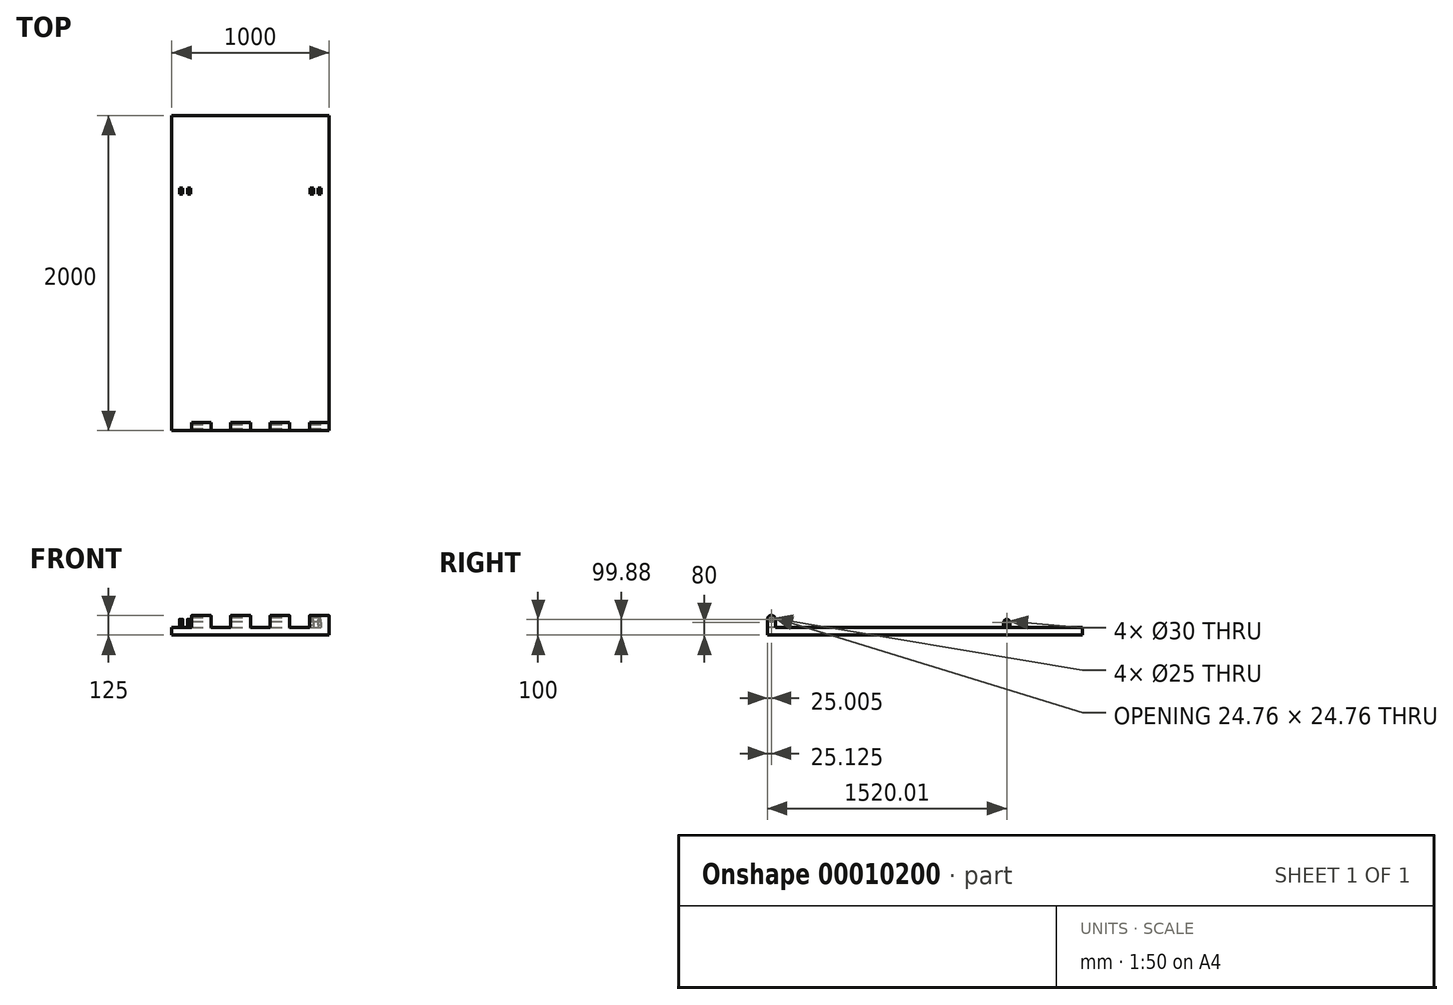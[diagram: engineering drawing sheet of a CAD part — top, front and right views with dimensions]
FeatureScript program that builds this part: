
annotation { "Feature Type Name" : "Feature", "Feature Type Description" : "" }
export const myFeature = defineFeature(function(context is Context, id is Id, definition is map)
    precondition{}
    {
        {
            var Q0;
            Q0=qCreatedBy(makeId("Top.planeOp"),FACE);
            var sketch = newSketch(context, id + "F0", { "sketchPlane" : qUnion([Q0])});
            skLineSegment(sketch, "E0.bottom", {"start": v(-409.07, -956.56) * mm, "end": v(590.93, -956.56) * mm});
            skLineSegment(sketch, "E0.top", {"start": v(-409.07, 1043.44) * mm, "end": v(590.93, 1043.44) * mm});
            skLineSegment(sketch, "E0.left", {"start": v(-409.07, -956.56) * mm, "end": v(-409.07, 1043.44) * mm});
            skLineSegment(sketch, "E0.right", {"start": v(590.93, -956.56) * mm, "end": v(590.93, 1043.44) * mm});
            skSolve(sketch);
        }
        {
            var Q0;
            Q0=qSketchRegion(id+"F0",true);
            extrude(context, id + "F1", {"entities" : qUnion([Q0]), "depth" : 50 * mm});
        }
        {
            var Q0;
            Q0=makeQuery(id+"F1.opExtrude","SWEPT_FACE",FACE,{"disambiguationData":[OSD([sQuery(id+"F0.wireOp",EDGE,"E0.right")])]});
            var sketch = newSketch(context, id + "F2", { "sketchPlane" : qUnion([Q0])});
            skLineSegment(sketch, "E1.bottom", {"start": v(-956.56, 50) * mm, "end": v(-906.56, 50) * mm});
            skLineSegment(sketch, "E1.left", {"start": v(-956.56, 50) * mm, "end": v(-956.56, 100) * mm});
            skLineSegment(sketch, "E1.right", {"start": v(-906.56, 50) * mm, "end": v(-906.56, 100) * mm});
            skArc(sketch, "E2", {"start": v(-906.56, 100) * mm, "mid": v(-931.56, 125) * mm, "end": v(-956.56, 100) * mm});
            skCircle(sketch, "E3", {"center": v(-931.56, 100) * mm, "radius": 12.5 * mm});
            skSolve(sketch);
        }
        {
            var Q0;
            Q0=qSketchRegion(id+"F2",true);
            extrude(context, id + "F3", {"entities" : qUnion([Q0]), "oppositeDirection" : true, "depth" : 1000 * mm});
        }
        {
            var Q0;
            Q0=makeQuery(id+"F1.opExtrude","CAP_FACE",FACE,{"disambiguationData":[OSD([sQuery(id+"F0.wireOp",EDGE,"E0.bottom"),sQuery(id+"F0.wireOp",EDGE,"E0.top"),sQuery(id+"F0.wireOp",EDGE,"E0.left"),sQuery(id+"F0.wireOp",EDGE,"E0.right")])],"isStart":false});
            var sketch = newSketch(context, id + "F4", { "sketchPlane" : qUnion([Q0])});
            skLineSegment(sketch, "E4.bottom", {"start": v(-159.07, -818.58) * mm, "end": v(-34.07, -818.58) * mm});
            skLineSegment(sketch, "E4.top", {"start": v(-159.07, -1033.47) * mm, "end": v(-34.07, -1033.47) * mm});
            skLineSegment(sketch, "E4.left", {"start": v(-159.07, -818.58) * mm, "end": v(-159.07, -1033.47) * mm});
            skLineSegment(sketch, "E4.right", {"start": v(-34.07, -818.58) * mm, "end": v(-34.07, -1033.47) * mm});
            skLineSegment(sketch, "E5.bottom", {"start": v(90.93, -816.35) * mm, "end": v(215.93, -816.35) * mm});
            skLineSegment(sketch, "E5.top", {"start": v(90.93, -1023.71) * mm, "end": v(215.93, -1023.71) * mm});
            skLineSegment(sketch, "E5.left", {"start": v(90.93, -816.35) * mm, "end": v(90.93, -1023.71) * mm});
            skLineSegment(sketch, "E5.right", {"start": v(215.93, -816.35) * mm, "end": v(215.93, -1023.71) * mm});
            skLineSegment(sketch, "E6.bottom", {"start": v(340.93, -840.14) * mm, "end": v(465.93, -840.14) * mm});
            skLineSegment(sketch, "E6.top", {"start": v(340.93, -1023.71) * mm, "end": v(465.93, -1023.71) * mm});
            skLineSegment(sketch, "E6.left", {"start": v(340.93, -840.14) * mm, "end": v(340.93, -1023.71) * mm});
            skLineSegment(sketch, "E6.right", {"start": v(465.93, -840.14) * mm, "end": v(465.93, -1023.71) * mm});
            skLineSegment(sketch, "E7.bottom", {"start": v(-284.07, -802.65) * mm, "end": v(-409.07, -802.65) * mm});
            skLineSegment(sketch, "E7.top", {"start": v(-284.07, -1062.3) * mm, "end": v(-409.07, -1062.3) * mm});
            skLineSegment(sketch, "E7.left", {"start": v(-284.07, -802.65) * mm, "end": v(-284.07, -1062.3) * mm});
            skLineSegment(sketch, "E7.right", {"start": v(-409.07, -802.65) * mm, "end": v(-409.07, -1062.3) * mm});
            skSolve(sketch);
        }
        {
            var Q0;
            Q0=qSketchRegion(id+"F4",true);
            extrude(context, id + "F5", {"entities" : qUnion([Q0]), "operationType" : NewBodyOperationType.REMOVE, "endBound" : BoundingType.THROUGH_ALL, "depth" : 60 * mm});
        }
        {
            var Q0;
            Q0=makeQuery(id+"F1.opExtrude","SWEPT_BODY",BODY,{"disambiguationData":[OSD([sQuery(id+"F0.wireOp",EDGE,"E0.bottom"),sQuery(id+"F0.wireOp",EDGE,"E0.top"),sQuery(id+"F0.wireOp",EDGE,"E0.left"),sQuery(id+"F0.wireOp",EDGE,"E0.right")])]});
            var Q1;
            Q1=makeQuery(id+"F5.boolean.opBoolean","SPLIT",BODY,{"disambiguationData":[OD(0.0)],"derivedFrom":makeQuery(id+"F3.opExtrude","SWEPT_BODY",BODY,{"disambiguationData":[OSD([sQuery(id+"F2.wireOp",EDGE,"E1.bottom"),sQuery(id+"F2.wireOp",EDGE,"E1.left"),sQuery(id+"F2.wireOp",EDGE,"E1.right"),sQuery(id+"F2.wireOp",EDGE,"E2"),sQuery(id+"F2.wireOp",EDGE,"E3")])]})});
            var Q2;
            Q2=makeQuery(id+"F5.boolean.opBoolean","SPLIT",BODY,{"disambiguationData":[OD(1.0)],"derivedFrom":makeQuery(id+"F3.opExtrude","SWEPT_BODY",BODY,{"disambiguationData":[OSD([sQuery(id+"F2.wireOp",EDGE,"E1.bottom"),sQuery(id+"F2.wireOp",EDGE,"E1.left"),sQuery(id+"F2.wireOp",EDGE,"E1.right"),sQuery(id+"F2.wireOp",EDGE,"E2"),sQuery(id+"F2.wireOp",EDGE,"E3")])]})});
            var Q3;
            Q3=makeQuery(id+"F5.boolean.opBoolean","SPLIT",BODY,{"disambiguationData":[OD(2.0)],"derivedFrom":makeQuery(id+"F3.opExtrude","SWEPT_BODY",BODY,{"disambiguationData":[OSD([sQuery(id+"F2.wireOp",EDGE,"E1.bottom"),sQuery(id+"F2.wireOp",EDGE,"E1.left"),sQuery(id+"F2.wireOp",EDGE,"E1.right"),sQuery(id+"F2.wireOp",EDGE,"E2"),sQuery(id+"F2.wireOp",EDGE,"E3")])]})});
            booleanBodies(context, id + "F6", {"operationType" : BooleanOperationType.UNION, "tools" : qUnion([Q0, Q1, Q2, Q3])});
        }
        {
            var Q0;
            Q0=makeQuery(id+"F6.opBoolean","MERGE",FACE,{"derivedFrom":[makeQuery(id+"F1.opExtrude","SWEPT_FACE",FACE,{"disambiguationData":[OSD([sQuery(id+"F0.wireOp",EDGE,"E0.right")])]}),makeQuery(id+"F3.opExtrude","CAP_FACE",FACE,{"disambiguationData":[OSD([sQuery(id+"F2.wireOp",EDGE,"E1.bottom"),sQuery(id+"F2.wireOp",EDGE,"E1.left"),sQuery(id+"F2.wireOp",EDGE,"E1.right"),sQuery(id+"F2.wireOp",EDGE,"E2"),sQuery(id+"F2.wireOp",EDGE,"E3")])],"isStart":true})]});
            var sketch = newSketch(context, id + "F7", { "sketchPlane" : qUnion([Q0])});
            skLineSegment(sketch, "E8.bottom", {"start": v(543.44, 50) * mm, "end": v(583.44, 50) * mm});
            skLineSegment(sketch, "E8.left", {"start": v(543.44, 50) * mm, "end": v(543.44, 80) * mm});
            skLineSegment(sketch, "E8.right", {"start": v(583.44, 50) * mm, "end": v(583.44, 80) * mm});
            skArc(sketch, "E9", {"start": v(583.44, 80) * mm, "mid": v(563.44, 100) * mm, "end": v(543.44, 80) * mm});
            skCircle(sketch, "E10", {"center": v(563.44, 80) * mm, "radius": 15 * mm});
            skSolve(sketch);
        }
        {
            var Q0;
            Q0=qSketchRegion(id+"F7",true);
            extrude(context, id + "F8", {"entities" : qUnion([Q0]), "oppositeDirection" : true, "depth" : 1000 * mm});
        }
        {
            var Q0;
            Q0=makeQuery(id+"F8.opExtrude","SWEPT_FACE",FACE,{"disambiguationData":[OSD([sQuery(id+"F7.wireOp",EDGE,"E8.bottom")])]});
            var sketch = newSketch(context, id + "F9", { "sketchPlane" : qUnion([Q0])});
            skLineSegment(sketch, "E11.bottom", {"start": v(590.93, -583.44) * mm, "end": v(540.93, -583.44) * mm});
            skLineSegment(sketch, "E11.top", {"start": v(590.93, -383.44) * mm, "end": v(540.93, -383.44) * mm});
            skLineSegment(sketch, "E11.left", {"start": v(590.93, -583.44) * mm, "end": v(590.93, -383.44) * mm});
            skLineSegment(sketch, "E11.right", {"start": v(540.93, -583.44) * mm, "end": v(540.93, -383.44) * mm});
            skLineSegment(sketch, "E12.bottom", {"start": v(520.93, -583.44) * mm, "end": v(490.93, -583.44) * mm});
            skLineSegment(sketch, "E12.top", {"start": v(520.93, -383.44) * mm, "end": v(490.93, -383.44) * mm});
            skLineSegment(sketch, "E12.left", {"start": v(520.93, -583.44) * mm, "end": v(520.93, -383.44) * mm});
            skLineSegment(sketch, "E12.right", {"start": v(490.93, -583.44) * mm, "end": v(490.93, -383.44) * mm});
            skLineSegment(sketch, "E13.bottom", {"start": v(470.93, -383.44) * mm, "end": v(-289.07, -383.44) * mm});
            skLineSegment(sketch, "E13.top", {"start": v(470.93, -583.44) * mm, "end": v(-289.07, -583.44) * mm});
            skLineSegment(sketch, "E13.left", {"start": v(470.93, -583.44) * mm, "end": v(470.93, -383.44) * mm});
            skLineSegment(sketch, "E13.right", {"start": v(-289.07, -583.44) * mm, "end": v(-289.07, -383.44) * mm});
            skLineSegment(sketch, "E14.bottom", {"start": v(-359.07, -583.44) * mm, "end": v(-409.07, -583.44) * mm});
            skLineSegment(sketch, "E14.top", {"start": v(-359.07, -383.44) * mm, "end": v(-409.07, -383.44) * mm});
            skLineSegment(sketch, "E14.left", {"start": v(-359.07, -583.44) * mm, "end": v(-359.07, -383.44) * mm});
            skLineSegment(sketch, "E14.right", {"start": v(-409.07, -583.44) * mm, "end": v(-409.07, -383.44) * mm});
            skLineSegment(sketch, "E15.bottom", {"start": v(-309.07, -583.44) * mm, "end": v(-339.07, -583.44) * mm});
            skLineSegment(sketch, "E15.top", {"start": v(-309.07, -383.44) * mm, "end": v(-339.07, -383.44) * mm});
            skLineSegment(sketch, "E15.left", {"start": v(-309.07, -583.44) * mm, "end": v(-309.07, -383.44) * mm});
            skLineSegment(sketch, "E15.right", {"start": v(-339.07, -583.44) * mm, "end": v(-339.07, -383.44) * mm});
            skSolve(sketch);
        }
        {
            var Q0;
            Q0=qSketchRegion(id+"F9",true);
            extrude(context, id + "F10", {"entities" : qUnion([Q0]), "operationType" : NewBodyOperationType.REMOVE, "endBound" : BoundingType.THROUGH_ALL, "oppositeDirection" : true, "depth" : 25 * mm});
        }
    });
